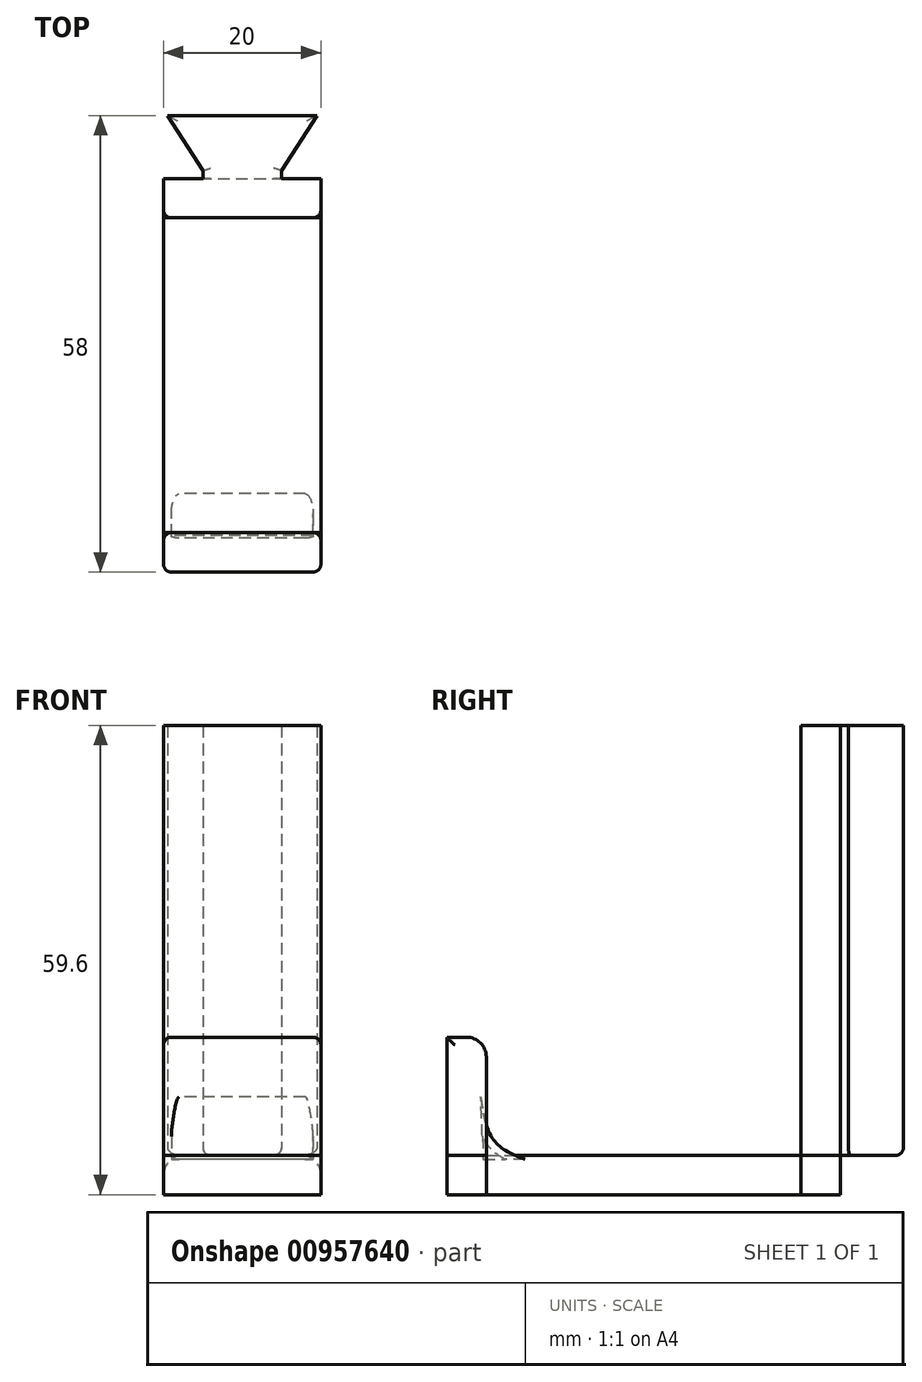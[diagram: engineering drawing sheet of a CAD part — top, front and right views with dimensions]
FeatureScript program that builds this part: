
annotation { "Feature Type Name" : "Feature", "Feature Type Description" : "" }
export const myFeature = defineFeature(function(context is Context, id is Id, definition is map)
    precondition{}
    {
        {
            var Q0;
            Q0=qCreatedBy(makeId("Top.planeOp"),FACE);
            var sketch = newSketch(context, id + "F0", { "sketchPlane" : qUnion([Q0])});
            skLineSegment(sketch, "E0.bottom", {"start": v(0, 0) * mm, "end": v(20, 0) * mm});
            skLineSegment(sketch, "E0.top", {"start": v(0, 5) * mm, "end": v(20, 5) * mm});
            skLineSegment(sketch, "E0.left", {"start": v(0, 0) * mm, "end": v(0, 5) * mm});
            skLineSegment(sketch, "E0.right", {"start": v(20, 0) * mm, "end": v(20, 5) * mm});
            skLineSegment(sketch, "E1.top", {"start": v(0, 50) * mm, "end": v(20, 50) * mm});
            skLineSegment(sketch, "E1.left", {"start": v(0, 5) * mm, "end": v(0, 50) * mm});
            skLineSegment(sketch, "E1.right", {"start": v(20, 5) * mm, "end": v(20, 50) * mm});
            skLineSegment(sketch, "E2.top", {"start": v(0, 45) * mm, "end": v(20, 45) * mm});
            skLineSegment(sketch, "E2.left", {"start": v(0, 50) * mm, "end": v(0, 45) * mm});
            skLineSegment(sketch, "E2.right", {"start": v(20, 50) * mm, "end": v(20, 45) * mm});
            skLineSegment(sketch, "E3.bottom", {"start": v(5, 50) * mm, "end": v(15, 50) * mm});
            skLineSegment(sketch, "E3.top", {"start": v(5, 51) * mm, "end": v(15, 51) * mm});
            skLineSegment(sketch, "E3.left", {"start": v(5, 50) * mm, "end": v(5, 51) * mm});
            skLineSegment(sketch, "E3.right", {"start": v(15, 50) * mm, "end": v(15, 51) * mm});
            skLineSegment(sketch, "E4", {"start": v(19.5, 58) * mm, "end": v(15, 51) * mm});
            skLineSegment(sketch, "E5", {"start": v(5, 51) * mm, "end": v(0.5, 58) * mm});
            skLineSegment(sketch, "E6", {"start": v(0.5, 58) * mm, "end": v(19.5, 58) * mm});
            skSolve(sketch);
        }
        {
            var Q0;
            Q0=makeQuery(id+"F0.imprint","IMPRINT",FACE,{"disambiguationData":[TD([[makeQuery(id+"F0.imprint","IMPRINT",EDGE,{"derivedFrom":sQuery(id+"F0.wireOp",EDGE,"E3.top")}),1.0]])]});
            var Q1;
            Q1=makeQuery(id+"F0.imprint","IMPRINT",FACE,{"disambiguationData":[TD([[makeQuery(id+"F0.imprint","IMPRINT",EDGE,{"derivedFrom":sQuery(id+"F0.wireOp",EDGE,"E3.top")}),-1.0]])]});
            var Q2;
            {var subQ3=sQuery(id+"F0.wireOp",EDGE,"E2.top");Q2=makeQuery(id+"F0.imprint","IMPRINT",FACE,{"disambiguationData":[TD([[makeQuery(id+"F0.imprint","IMPRINT",EDGE,{"derivedFrom":subQ3}),1.0]])]});}
            extrude(context, id + "F1", {"entities" : qUnion([Q0, Q1, Q2]), "depth" : 59.6 * mm, "offsetDistance" : 25 * mm, "hasSecondDirection" : true, "secondDirectionOppositeDirection" : false, "secondDirectionDepth" : 5 * mm});
        }
        {
            var Q0;
            {var subQ3=sQuery(id+"F0.wireOp",EDGE,"E2.top");Q0=makeQuery(id+"F0.imprint","IMPRINT",FACE,{"disambiguationData":[TD([[makeQuery(id+"F0.imprint","IMPRINT",EDGE,{"derivedFrom":subQ3}),1.0]])]});}
            extrude(context, id + "F2", {"entities" : qUnion([Q0]), "operationType" : NewBodyOperationType.ADD, "depth" : 59.6 * mm, "offsetDistance" : 25 * mm, "hasSecondDirection" : true, "secondDirectionOppositeDirection" : false, "secondDirectionDepth" : 5 * mm});
        }
        {
            var Q0;
            Q0=makeQuery(id+"F0.imprint","IMPRINT",FACE,{"disambiguationData":[TD([[makeQuery(id+"F0.imprint","IMPRINT",EDGE,{"derivedFrom":sQuery(id+"F0.wireOp",EDGE,"E0.bottom")}),1.0]])]});
            extrude(context, id + "F3", {"entities" : qUnion([Q0]), "depth" : 20 * mm, "offsetDistance" : 25 * mm, "hasSecondDirection" : true, "secondDirectionOppositeDirection" : false, "secondDirectionDepth" : 5 * mm});
        }
        {
            var Q0;
            {var subQ0=sQuery(id+"F0.wireOp",EDGE,"E0.top");Q0=makeQuery(id+"F0.imprint","IMPRINT",FACE,{"disambiguationData":[TD([[makeQuery(id+"F0.imprint","IMPRINT",EDGE,{"derivedFrom":subQ0}),1.0]])]});}
            extrude(context, id + "F4", {"entities" : qUnion([Q0]), "depth" : 5 * mm, "offsetDistance" : 25 * mm});
        }
        {
            var Q0;
            Q0=makeQuery(id+"F0.imprint","IMPRINT",FACE,{"disambiguationData":[TD([[makeQuery(id+"F0.imprint","IMPRINT",EDGE,{"derivedFrom":sQuery(id+"F0.wireOp",EDGE,"E0.bottom")}),1.0]])]});
            var Q1;
            {var subQ3=sQuery(id+"F0.wireOp",EDGE,"E2.top");Q1=makeQuery(id+"F0.imprint","IMPRINT",FACE,{"disambiguationData":[TD([[makeQuery(id+"F0.imprint","IMPRINT",EDGE,{"derivedFrom":subQ3}),1.0]])]});}
            extrude(context, id + "F5", {"entities" : qUnion([Q0, Q1]), "depth" : 5 * mm, "offsetDistance" : 25 * mm});
        }
        {
            var Q0;
            Q0=makeQuery(id+"F4.opExtrude","CAP_EDGE",EDGE,{"disambiguationData":[OSD([sQuery(id+"F0.wireOp",EDGE,"E1.right")])],"isStart":false});
            var Q1;
            Q1=makeQuery(id+"F4.opExtrude","CAP_EDGE",EDGE,{"disambiguationData":[OSD([sQuery(id+"F0.wireOp",EDGE,"E1.left")])],"isStart":false});
            var Q2;
            Q2=makeQuery(id+"F3.opExtrude","CAP_EDGE",EDGE,{"disambiguationData":[OSD([sQuery(id+"F0.wireOp",EDGE,"E0.top")])],"isStart":false});
            fillet(context, id + "F6", {"entities" : qUnion([Q0, Q1, Q2]), "radius" : 2.5 * mm, "tangentPropagation" : true, "allowEdgeOverflow" : false});
        }
        {
            var Q0;
            Q0=qCreatedBy(makeId("Right.planeOp"),FACE);
            var sketch = newSketch(context, id + "F7", { "sketchPlane" : qUnion([Q0])});
            skLineSegment(sketch, "E7", {"start": v(0, 0) * mm, "end": v(13.13, 0) * mm});
            skLineSegment(sketch, "E8", {"start": v(13.13, 0) * mm, "end": v(0, 18.46) * mm});
            skLineSegment(sketch, "E9", {"start": v(0, 18.46) * mm, "end": v(0, 0) * mm});
            skFitSpline(sketch, "E10", {"points": [v(4.3, 12.42) * mm, v(5.98, 6.87) * mm, v(9.94, 4.48) * mm], "startDerivative": vector(1.82, -11.94) * mm, "endDerivative": vector(9.6, -3.78) * mm});
            skLineSegment(sketch, "E11", {"start": v(4.3, 12.42) * mm, "end": v(4.62, 4.48) * mm});
            skLineSegment(sketch, "E12", {"start": v(4.62, 4.48) * mm, "end": v(9.94, 4.48) * mm});
            skPoint(sketch, "E13.orphan", {"position": v(6.08, 4.48) * mm});
            skSolve(sketch);
        }
        {
            var Q0;
            Q0=makeQuery(id+"F7.imprint","IMPRINT",FACE,{"disambiguationData":[TD([[makeQuery(id+"F7.imprint","IMPRINT",EDGE,{"derivedFrom":sQuery(id+"F7.wireOp",EDGE,"E10")}),-1.0]])]});
            extrude(context, id + "F8", {"entities" : qUnion([Q0]), "depth" : 19 * mm, "offsetDistance" : 25 * mm, "hasSecondDirection" : true, "secondDirectionOppositeDirection" : false, "secondDirectionDepth" : 1 * mm});
        }
        {
            var Q0;
            Q0=makeQuery(id+"F3.opExtrude","SWEPT_EDGE",EDGE,{"disambiguationData":[OSD([sQuery(id+"F0.wireOp",EDGE,"E0.top"),sQuery(id+"F0.wireOp",EDGE,"E0.right"),sQuery(id+"F0.wireOp",EDGE,"E1.right")])]});
            var Q1;
            Q1=makeQuery(id+"F3.opExtrude","SWEPT_EDGE",EDGE,{"disambiguationData":[OSD([sQuery(id+"F0.wireOp",EDGE,"E0.top"),sQuery(id+"F0.wireOp",EDGE,"E0.left"),sQuery(id+"F0.wireOp",EDGE,"E1.left")])]});
            var Q2;
            Q2=makeQuery(id+"F2.opExtrude","SWEPT_EDGE",EDGE,{"disambiguationData":[OSD([sQuery(id+"F0.wireOp",EDGE,"E1.left"),sQuery(id+"F0.wireOp",EDGE,"E2.top"),sQuery(id+"F0.wireOp",EDGE,"E2.left")])]});
            var Q3;
            Q3=makeQuery(id+"F1.opExtrude","CAP_EDGE",EDGE,{"disambiguationData":[OSD([sQuery(id+"F0.wireOp",EDGE,"0AZJ9n3G-vqmL-AJ7P-NQpQ-ZTYbRNAHJxr4")])],"isStart":true});
            var Q4;
            Q4=makeQuery(id+"F1.opExtrude","CAP_EDGE",EDGE,{"disambiguationData":[OSD([sQuery(id+"F0.wireOp",EDGE,"gg1rdKDO-KxFh-CbF8-zYYj-SX4EOiL4Fdvu")])],"isStart":true});
            var Q5;
            Q5=makeQuery(id+"F1.opExtrude","CAP_EDGE",EDGE,{"disambiguationData":[OSD([sQuery(id+"F0.wireOp",EDGE,"4xYDmxTQ-vGwR-nJFe-dzzj-uoGl0i99mpgP")])],"isStart":true});
            var Q6;
            Q6=makeQuery(id+"F2.opExtrude","CAP_EDGE",EDGE,{"disambiguationData":[OSD([sQuery(id+"F0.wireOp",EDGE,"E2.top")])],"isStart":false});
            var Q7;
            Q7=makeQuery(id+"F2.opExtrude","CAP_EDGE",EDGE,{"disambiguationData":[OSD([sQuery(id+"F0.wireOp",EDGE,"E2.right")])],"isStart":false});
            var Q8;
            Q8=makeQuery(id+"F2.opExtrude","CAP_EDGE",EDGE,{"disambiguationData":[OSD([sQuery(id+"F0.wireOp",EDGE,"E2.left")])],"isStart":false});
            var Q9;
            Q9=makeQuery(id+"F6.opFillet","BLEND_EDGE",EDGE,{"blendedFrom":[makeQuery(id+"F3.opExtrude","CAP_EDGE",EDGE,{"disambiguationData":[OSD([sQuery(id+"F0.wireOp",EDGE,"E0.top")])],"isStart":false}),makeQuery(id+"F3.opExtrude","SWEPT_FACE",FACE,{"disambiguationData":[OSD([sQuery(id+"F0.wireOp",EDGE,"E0.bottom")])]})],"blendedInto":[makeQuery(id+"F3.opExtrude","SWEPT_FACE",FACE,{"disambiguationData":[OSD([sQuery(id+"F0.wireOp",EDGE,"E0.bottom")])]})]});
            var Q10;
            Q10=makeQuery(id+"F3.opExtrude","SWEPT_EDGE",EDGE,{"disambiguationData":[OSD([sQuery(id+"F0.wireOp",EDGE,"E0.bottom"),sQuery(id+"F0.wireOp",EDGE,"E0.left")])]});
            var Q11;
            Q11=makeQuery(id+"F3.opExtrude","SWEPT_EDGE",EDGE,{"disambiguationData":[OSD([sQuery(id+"F0.wireOp",EDGE,"E0.bottom"),sQuery(id+"F0.wireOp",EDGE,"E0.right")])]});
            var Q12;
            Q12=makeQuery(id+"F8.opExtrude","CAP_EDGE",EDGE,{"disambiguationData":[OSD([sQuery(id+"F7.wireOp",EDGE,"E10")])],"isStart":true});
            var Q13;
            Q13=makeQuery(id+"F8.opExtrude","CAP_EDGE",EDGE,{"disambiguationData":[OSD([sQuery(id+"F7.wireOp",EDGE,"E10")])],"isStart":false});
            var Q14;
            Q14=makeQuery(id+"F2.opExtrude","SWEPT_EDGE",EDGE,{"disambiguationData":[OSD([sQuery(id+"F0.wireOp",EDGE,"E1.right"),sQuery(id+"F0.wireOp",EDGE,"E2.top"),sQuery(id+"F0.wireOp",EDGE,"E2.right")])]});
            var Q15;
            Q15=makeQuery(id+"F5.opExtrude","SWEPT_EDGE",EDGE,{"disambiguationData":[OSD([sQuery(id+"F0.wireOp",EDGE,"E0.bottom"),sQuery(id+"F0.wireOp",EDGE,"E0.right")])]});
            var Q16;
            Q16=makeQuery(id+"F5.opExtrude","SWEPT_EDGE",EDGE,{"disambiguationData":[OSD([sQuery(id+"F0.wireOp",EDGE,"E0.bottom"),sQuery(id+"F0.wireOp",EDGE,"E0.left")])]});
            fillet(context, id + "F9", {"entities" : qUnion([Q0, Q1, Q2, Q3, Q4, Q5, Q6, Q7, Q8, Q9, Q10, Q11, Q12, Q13, Q14, Q15, Q16]), "radius" : 1 * mm, "tangentPropagation" : true, "allowEdgeOverflow" : false});
        }
        {
            var Q0;
            Q0=makeQuery(id+"F1.opExtrude","CAP_EDGE",EDGE,{"disambiguationData":[OSD([sQuery(id+"F0.wireOp",EDGE,"E6")])],"isStart":true});
            var Q1;
            Q1=makeQuery(id+"F1.opExtrude","CAP_EDGE",EDGE,{"disambiguationData":[OSD([sQuery(id+"F0.wireOp",EDGE,"E5")])],"isStart":true});
            var Q2;
            Q2=makeQuery(id+"F1.opExtrude","CAP_EDGE",EDGE,{"disambiguationData":[OSD([sQuery(id+"F0.wireOp",EDGE,"E4")])],"isStart":true});
            var Q3;
            Q3=makeQuery(id+"F1.opExtrude","CAP_EDGE",EDGE,{"disambiguationData":[OSD([sQuery(id+"F0.wireOp",EDGE,"E3.right")])],"isStart":true});
            var Q4;
            Q4=makeQuery(id+"F1.opExtrude","CAP_EDGE",EDGE,{"disambiguationData":[OSD([sQuery(id+"F0.wireOp",EDGE,"E3.left")])],"isStart":true});
            var Q5;
            Q5=makeQuery(id+"F1.opExtrude","SWEPT_EDGE",EDGE,{"disambiguationData":[OSD([sQuery(id+"F0.wireOp",EDGE,"E1.right"),sQuery(id+"F0.wireOp",EDGE,"E2.top")])]});
            var Q6;
            Q6=makeQuery(id+"F1.opExtrude","SWEPT_EDGE",EDGE,{"disambiguationData":[OSD([sQuery(id+"F0.wireOp",EDGE,"E1.left"),sQuery(id+"F0.wireOp",EDGE,"E2.top")])]});
            fillet(context, id + "F10", {"entities" : qUnion([Q0, Q1, Q2, Q3, Q4, Q5, Q6]), "radius" : 1 * mm, "tangentPropagation" : true, "allowEdgeOverflow" : false});
        }
    });
